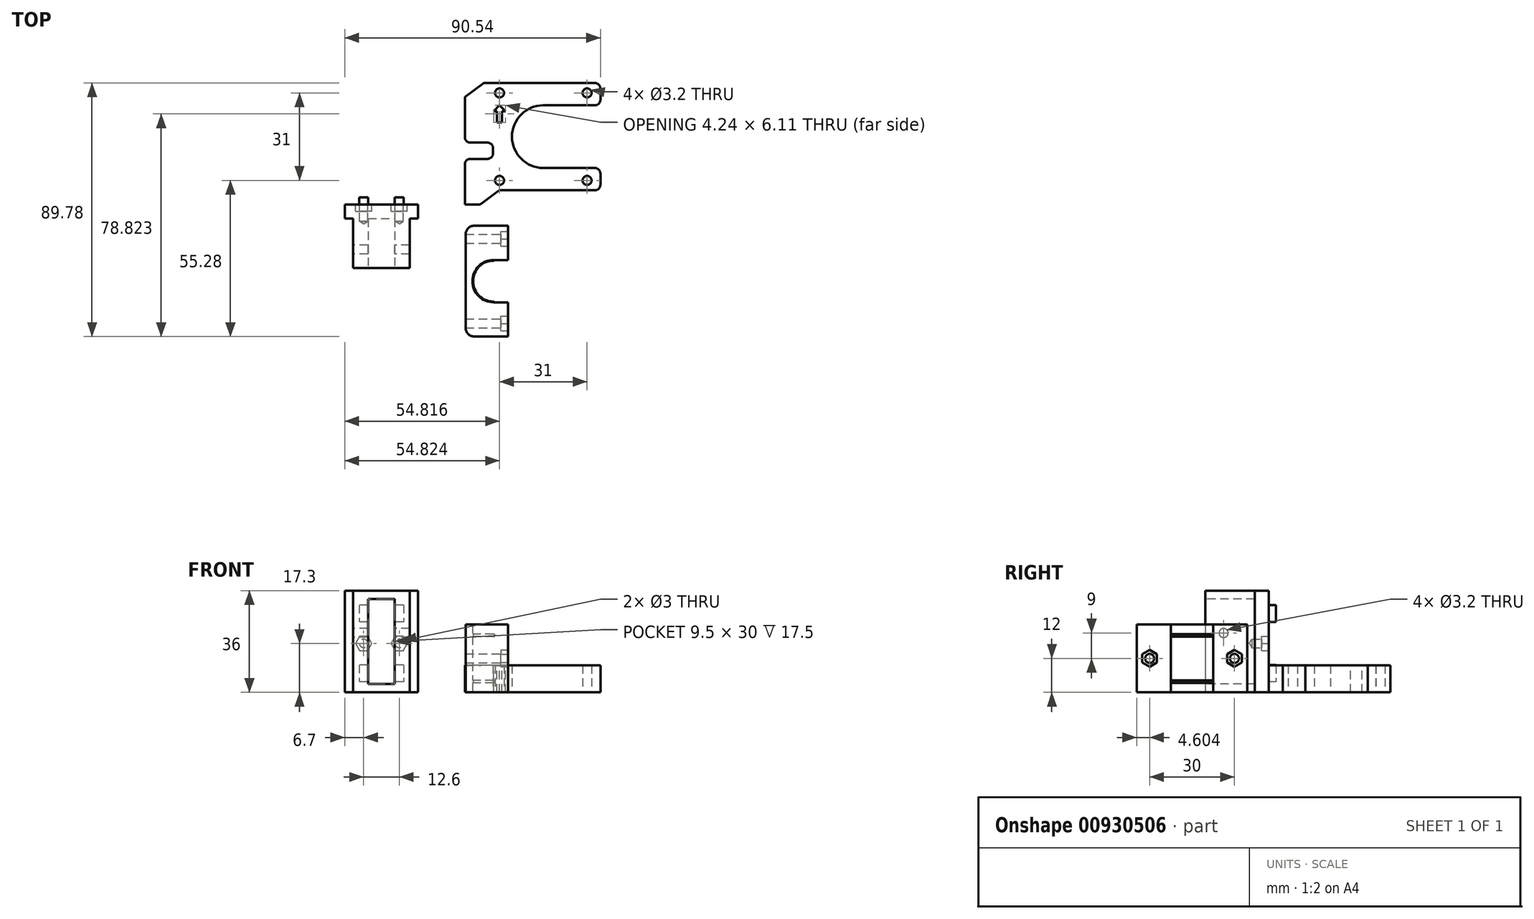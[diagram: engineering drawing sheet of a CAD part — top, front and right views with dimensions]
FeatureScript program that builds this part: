
annotation { "Feature Type Name" : "Feature", "Feature Type Description" : "" }
export const myFeature = defineFeature(function(context is Context, id is Id, definition is map)
    precondition{}
    {
        {
            assignVariable(context, id + "F0", {"name" : "Tolerance", "anyValue" : 0.2});
        }
        {
            var Q0;
            Q0=qCreatedBy(makeId("Top.planeOp"),FACE);
            var sketch = newSketch(context, id + "F1", { "sketchPlane" : qUnion([Q0])});
            skLineSegment(sketch, "E0", {"start": v(7, 16.12) * mm, "end": v(3, 16.12) * mm});
            skLineSegment(sketch, "E1", {"start": v(0, 4.53) * mm, "end": v(0, 0) * mm});
            skLineSegment(sketch, "E2", {"start": v(0, 0) * mm, "end": v(5.2, 0) * mm});
            skLineSegment(sketch, "E3", {"start": v(14.51, 5) * mm, "end": v(46, 5) * mm});
            skArc(sketch, "E4", {"start": v(46, 5) * mm, "mid": v(47.41, 5.59) * mm, "end": v(48, 7) * mm});
            skArc(sketch, "E5", {"start": v(48, 41) * mm, "mid": v(47.41, 42.41) * mm, "end": v(46, 43) * mm});
            skLineSegment(sketch, "E6", {"start": v(46, 43) * mm, "end": v(8.98, 43) * mm});
            skLineSegment(sketch, "E7", {"start": v(3, 21.87) * mm, "end": v(7, 21.87) * mm});
            skCircle(sketch, "E8", {"center": v(12.28, 39.5) * mm, "radius": 1.6 * mm});
            skCircle(sketch, "E9", {"center": v(43.28, 39.5) * mm, "radius": 1.6 * mm});
            skCircle(sketch, "E10", {"center": v(12.28, 8.5) * mm, "radius": 1.6 * mm});
            skCircle(sketch, "E11", {"center": v(43.28, 8.5) * mm, "radius": 1.6 * mm});
            skLineSegment(sketch, "E12", {"start": v(6.37, 42.8) * mm, "end": v(0, 38) * mm});
            skLineSegment(sketch, "E13", {"start": v(11.9, 4.8) * mm, "end": v(5.8, 0.2) * mm});
            skArc(sketch, "E14", {"start": v(6.98, 43) * mm, "mid": v(6.66, 42.95) * mm, "end": v(6.37, 42.8) * mm});
            skArc(sketch, "E15", {"start": v(12.51, 5) * mm, "mid": v(12.2, 4.95) * mm, "end": v(11.9, 4.8) * mm});
            skArc(sketch, "E16", {"start": v(5.2, 0) * mm, "mid": v(5.52, 0.05) * mm, "end": v(5.8, 0.2) * mm});
            skLineSegment(sketch, "E17", {"start": v(0, 38) * mm, "end": v(0, 33.47) * mm});
            skLineSegment(sketch, "E18", {"start": v(14.51, 5) * mm, "end": v(12.5, 5) * mm});
            skLineSegment(sketch, "E19", {"start": v(8.98, 43) * mm, "end": v(7.12, 43) * mm});
            skLineSegment(sketch, "E20", {"start": v(7.12, 43) * mm, "end": v(6.98, 43) * mm});
            skLineSegment(sketch, "E21", {"start": v(6.98, 43) * mm, "end": v(6.98, 43) * mm});
            skLineSegment(sketch, "E22", {"start": v(0, 4.53) * mm, "end": v(0, 12.27) * mm});
            skLineSegment(sketch, "E23", {"start": v(0, 25.73) * mm, "end": v(0, 33.47) * mm});
            skPoint(sketch, "E24", {"position": v(0, 16.12) * mm});
            skPoint(sketch, "E25", {"position": v(0, 21.87) * mm});
            skLineSegment(sketch, "E26", {"start": v(2, 16.12) * mm, "end": v(3, 16.12) * mm});
            skLineSegment(sketch, "E27", {"start": v(0, 14.12) * mm, "end": v(0, 12.27) * mm});
            skLineSegment(sketch, "E28", {"start": v(3, 21.87) * mm, "end": v(2, 21.87) * mm});
            skLineSegment(sketch, "E29", {"start": v(0, 25.73) * mm, "end": v(0, 23.87) * mm});
            skLineSegment(sketch, "E30", {"start": v(7, 16.12) * mm, "end": v(8, 16.12) * mm});
            skLineSegment(sketch, "E31", {"start": v(7, 21.87) * mm, "end": v(8, 21.87) * mm});
            skLineSegment(sketch, "E32", {"start": v(10, 18.12) * mm, "end": v(10, 19.87) * mm});
            skPoint(sketch, "E33", {"position": v(27.78, 12.9) * mm});
            skPoint(sketch, "E34", {"position": v(27.78, 35.1) * mm});
            skLineSegment(sketch, "E35", {"start": v(27.78, 35.1) * mm, "end": v(46, 35.1) * mm});
            skLineSegment(sketch, "E36", {"start": v(27.78, 12.9) * mm, "end": v(46, 12.9) * mm});
            skPoint(sketch, "E37", {"position": v(27.78, 24) * mm});
            skArc(sketch, "E38", {"start": v(27.78, 12.9) * mm, "mid": v(16.68, 24) * mm, "end": v(27.78, 35.1) * mm});
            skLineSegment(sketch, "E39", {"start": v(48, 10.9) * mm, "end": v(48, 7) * mm});
            skLineSegment(sketch, "E40", {"start": v(48, 37.1) * mm, "end": v(48, 41) * mm});
            skPoint(sketch, "E41.visualSharp", {"position": v(48, 12.9) * mm});
            skArc(sketch, "E41.filletArc", {"start": v(48, 10.9) * mm, "mid": v(47.41, 12.31) * mm, "end": v(46, 12.9) * mm});
            skPoint(sketch, "E42.visualSharp", {"position": v(48, 35.1) * mm});
            skArc(sketch, "E42.filletArc", {"start": v(46, 35.1) * mm, "mid": v(47.41, 35.69) * mm, "end": v(48, 37.1) * mm});
            skPoint(sketch, "E43.visualSharp", {"position": v(10, 16.12) * mm});
            skArc(sketch, "E43.filletArc", {"start": v(8, 16.12) * mm, "mid": v(9.41, 16.71) * mm, "end": v(10, 18.12) * mm});
            skPoint(sketch, "E44.visualSharp", {"position": v(10, 21.87) * mm});
            skArc(sketch, "E44.filletArc", {"start": v(10, 19.87) * mm, "mid": v(9.41, 21.29) * mm, "end": v(8, 21.87) * mm});
            skArc(sketch, "E45.filletArc", {"start": v(2, 16.12) * mm, "mid": v(0.59, 15.54) * mm, "end": v(0, 14.12) * mm});
            skArc(sketch, "E46.filletArc", {"start": v(0, 23.87) * mm, "mid": v(0.59, 22.46) * mm, "end": v(2, 21.87) * mm});
            skSolve(sketch);
        }
        {
            var Q0;
            Q0 = qSketchRegion(id + "F1", true);
            extrude(context, id + "F2", {"entities" : qUnion([Q0]), "depth" : 9.6 * mm, "offsetDistance" : 25 * mm});
        }
        {
            var Q0;
            Q0=makeQuery(id+"F2.opExtrude","CAP_FACE",FACE,{"disambiguationData":[OSD([sQuery(id+"F1.wireOp",EDGE,"E0"),sQuery(id+"F1.wireOp",EDGE,"E1"),sQuery(id+"F1.wireOp",EDGE,"E2"),sQuery(id+"F1.wireOp",EDGE,"E3"),sQuery(id+"F1.wireOp",EDGE,"E4"),sQuery(id+"F1.wireOp",EDGE,"E5"),sQuery(id+"F1.wireOp",EDGE,"E6"),sQuery(id+"F1.wireOp",EDGE,"E7"),sQuery(id+"F1.wireOp",EDGE,"E8"),sQuery(id+"F1.wireOp",EDGE,"E9"),sQuery(id+"F1.wireOp",EDGE,"E10"),sQuery(id+"F1.wireOp",EDGE,"E11"),sQuery(id+"F1.wireOp",EDGE,"E12"),sQuery(id+"F1.wireOp",EDGE,"E13"),sQuery(id+"F1.wireOp",EDGE,"E14"),sQuery(id+"F1.wireOp",EDGE,"E15"),sQuery(id+"F1.wireOp",EDGE,"E16"),sQuery(id+"F1.wireOp",EDGE,"E17"),sQuery(id+"F1.wireOp",EDGE,"E18"),sQuery(id+"F1.wireOp",EDGE,"E19"),sQuery(id+"F1.wireOp",EDGE,"E20"),sQuery(id+"F1.wireOp",EDGE,"E21"),sQuery(id+"F1.wireOp",EDGE,"E22"),sQuery(id+"F1.wireOp",EDGE,"E23"),sQuery(id+"F1.wireOp",EDGE,"E26"),sQuery(id+"F1.wireOp",EDGE,"E27"),sQuery(id+"F1.wireOp",EDGE,"E28"),sQuery(id+"F1.wireOp",EDGE,"E29"),sQuery(id+"F1.wireOp",EDGE,"E30"),sQuery(id+"F1.wireOp",EDGE,"E31"),sQuery(id+"F1.wireOp",EDGE,"E32"),sQuery(id+"F1.wireOp",EDGE,"E35"),sQuery(id+"F1.wireOp",EDGE,"E36"),sQuery(id+"F1.wireOp",EDGE,"E38"),sQuery(id+"F1.wireOp",EDGE,"E39"),sQuery(id+"F1.wireOp",EDGE,"E40"),sQuery(id+"F1.wireOp",EDGE,"E41.filletArc"),sQuery(id+"F1.wireOp",EDGE,"E42.filletArc"),sQuery(id+"F1.wireOp",EDGE,"E43.filletArc"),sQuery(id+"F1.wireOp",EDGE,"E44.filletArc"),sQuery(id+"F1.wireOp",EDGE,"E45.filletArc"),sQuery(id+"F1.wireOp",EDGE,"E46.filletArc")])],"isStart":false});
            var sketch = newSketch(context, id + "F3", { "sketchPlane" : qUnion([Q0])});
            skPoint(sketch, "E47", {"position": v(12.28, 39.5) * mm});
            skPoint(sketch, "E48", {"position": v(12.28, 35.1) * mm});
            skLineSegment(sketch, "E49", {"start": v(12.28, 35.1) * mm, "end": v(10.16, 32.99) * mm});
            skLineSegment(sketch, "E50", {"start": v(12.28, 35.1) * mm, "end": v(14.4, 32.97) * mm});
            skLineSegment(sketch, "E51", {"start": v(14.4, 32.97) * mm, "end": v(13.15, 32.97) * mm});
            skLineSegment(sketch, "E52", {"start": v(10.16, 32.99) * mm, "end": v(11.4, 32.99) * mm});
            skLineSegment(sketch, "E53", {"start": v(11.4, 32.99) * mm, "end": v(11.4, 28.99) * mm});
            skLineSegment(sketch, "E54", {"start": v(11.4, 28.99) * mm, "end": v(13.15, 28.99) * mm});
            skLineSegment(sketch, "E55", {"start": v(13.15, 28.99) * mm, "end": v(13.15, 32.97) * mm});
            skSolve(sketch);
        }
        {
            var Q0;
            Q0 = qSketchRegion(id + "F3", true);
            extrude(context, id + "F4", {"entities" : qUnion([Q0]), "operationType" : NewBodyOperationType.REMOVE, "endBound" : BoundingType.THROUGH_ALL, "oppositeDirection" : true, "depth" : 1 * mm, "offsetDistance" : 25 * mm});
        }
        {
            var Q0;
            Q0=qCreatedBy(makeId("Top.planeOp"),FACE);
            var sketch = newSketch(context, id + "F5", { "sketchPlane" : qUnion([Q0])});
            skLineSegment(sketch, "E56", {"start": v(15.27, -34.68) * mm, "end": v(10.17, -34.68) * mm});
            skArc(sketch, "E57", {"start": v(10.17, -19.68) * mm, "mid": v(2.67, -27.18) * mm, "end": v(10.17, -34.68) * mm});
            skLineSegment(sketch, "E58", {"start": v(10.17, -19.68) * mm, "end": v(15.27, -19.68) * mm});
            skLineSegment(sketch, "E59", {"start": v(15.27, -7.58) * mm, "end": v(3.26, -7.58) * mm});
            skArc(sketch, "E60", {"start": v(3.26, -7.58) * mm, "mid": v(1.14, -8.45) * mm, "end": v(0.26, -10.58) * mm});
            skLineSegment(sketch, "E61", {"start": v(0.26, -10.58) * mm, "end": v(0.26, -43.78) * mm});
            skArc(sketch, "E62", {"start": v(0.26, -43.78) * mm, "mid": v(1.14, -45.9) * mm, "end": v(3.26, -46.78) * mm});
            skLineSegment(sketch, "E63", {"start": v(3.26, -46.78) * mm, "end": v(15.27, -46.78) * mm});
            skLineSegment(sketch, "E64", {"start": v(15.27, -19.68) * mm, "end": v(15.27, -7.58) * mm});
            skLineSegment(sketch, "E65", {"start": v(15.27, -34.68) * mm, "end": v(15.27, -46.78) * mm});
            skSolve(sketch);
        }
        {
            var Q0;
            Q0=makeQuery(id+"F5.imprint","IMPRINT",FACE,{"disambiguationData":[TD([[makeQuery(id+"F5.imprint","IMPRINT",EDGE,{"derivedFrom":sQuery(id+"F5.wireOp",EDGE,"E56")}),1.0]])]});
            extrude(context, id + "F6", {"entities" : qUnion([Q0]), "depth" : (3.25 + getVariable(context, 'Tolerance') / 2) * mm, "offsetDistance" : 25 * mm});
        }
        {
            var Q0;
            Q0=makeQuery(id+"F6.opExtrude","CAP_FACE",FACE,{"disambiguationData":[OSD([sQuery(id+"F5.wireOp",EDGE,"E56"),sQuery(id+"F5.wireOp",EDGE,"E57"),sQuery(id+"F5.wireOp",EDGE,"E58"),sQuery(id+"F5.wireOp",EDGE,"E59"),sQuery(id+"F5.wireOp",EDGE,"E60"),sQuery(id+"F5.wireOp",EDGE,"E61"),sQuery(id+"F5.wireOp",EDGE,"E62"),sQuery(id+"F5.wireOp",EDGE,"E63"),sQuery(id+"F5.wireOp",EDGE,"E64"),sQuery(id+"F5.wireOp",EDGE,"E65")])],"isStart":false});
            var sketch = newSketch(context, id + "F7", { "sketchPlane" : qUnion([Q0])});
            skArc(sketch, "E66", {"start": v(10.17, -19.93) * mm, "mid": v(2.92, -27.18) * mm, "end": v(10.17, -34.43) * mm});
            skLineSegment(sketch, "E67", {"start": v(3.26, -7.58) * mm, "end": v(15.27, -7.58) * mm});
            skLineSegment(sketch, "E68", {"start": v(3.26, -46.78) * mm, "end": v(15.27, -46.78) * mm});
            skArc(sketch, "E69", {"start": v(3.26, -7.58) * mm, "mid": v(1.14, -8.45) * mm, "end": v(0.26, -10.58) * mm});
            skArc(sketch, "E70", {"start": v(3.26, -46.78) * mm, "mid": v(1.14, -45.9) * mm, "end": v(0.26, -43.78) * mm});
            skLineSegment(sketch, "E71", {"start": v(0.26, -43.78) * mm, "end": v(0.26, -10.58) * mm});
            skLineSegment(sketch, "E72", {"start": v(10.17, -34.43) * mm, "end": v(10.17, -34.68) * mm});
            skLineSegment(sketch, "E73", {"start": v(10.17, -34.68) * mm, "end": v(15.27, -34.68) * mm});
            skLineSegment(sketch, "E74", {"start": v(15.27, -34.68) * mm, "end": v(15.27, -46.78) * mm});
            skLineSegment(sketch, "E75", {"start": v(10.17, -19.93) * mm, "end": v(10.17, -19.68) * mm});
            skLineSegment(sketch, "E76", {"start": v(10.17, -19.68) * mm, "end": v(15.27, -19.68) * mm});
            skLineSegment(sketch, "E77", {"start": v(15.27, -19.68) * mm, "end": v(15.27, -7.58) * mm});
            skArc(sketch, "E78", {"start": v(10.17, -34.43) * mm, "mid": v(10.35, -34.5) * mm, "end": v(10.42, -34.68) * mm});
            skArc(sketch, "E79", {"start": v(10.17, -19.93) * mm, "mid": v(10.35, -19.85) * mm, "end": v(10.42, -19.68) * mm});
            skSolve(sketch);
        }
        {
            var Q0;
            Q0 = qSketchRegion(id + "F7", true);
            extrude(context, id + "F8", {"entities" : qUnion([Q0]), "operationType" : NewBodyOperationType.ADD, "depth" : (1.1 - getVariable(context, 'Tolerance')) * mm, "offsetDistance" : 25 * mm});
        }
        {
            var Q0;
            Q0=makeQuery(id+"F8.opExtrude","CAP_FACE",FACE,{"disambiguationData":[OSD([sQuery(id+"F7.wireOp",EDGE,"E66"),sQuery(id+"F7.wireOp",EDGE,"E67"),sQuery(id+"F7.wireOp",EDGE,"E68"),sQuery(id+"F7.wireOp",EDGE,"E69"),sQuery(id+"F7.wireOp",EDGE,"E70"),sQuery(id+"F7.wireOp",EDGE,"E71"),sQuery(id+"F7.wireOp",EDGE,"E73"),sQuery(id+"F7.wireOp",EDGE,"E74"),sQuery(id+"F7.wireOp",EDGE,"E76"),sQuery(id+"F7.wireOp",EDGE,"E77"),sQuery(id+"F7.wireOp",EDGE,"E78"),sQuery(id+"F7.wireOp",EDGE,"E79")])],"isStart":false});
            var sketch = newSketch(context, id + "F9", { "sketchPlane" : qUnion([Q0])});
            skArc(sketch, "E80", {"start": v(10.17, -19.68) * mm, "mid": v(2.67, -27.18) * mm, "end": v(10.17, -34.68) * mm});
            skLineSegment(sketch, "E81", {"start": v(10.17, -34.68) * mm, "end": v(15.27, -34.68) * mm});
            skLineSegment(sketch, "E82", {"start": v(10.17, -19.68) * mm, "end": v(15.27, -19.68) * mm});
            skLineSegment(sketch, "E83", {"start": v(15.27, -19.68) * mm, "end": v(15.27, -7.58) * mm});
            skLineSegment(sketch, "E84", {"start": v(15.27, -34.68) * mm, "end": v(15.27, -46.78) * mm});
            skLineSegment(sketch, "E85", {"start": v(15.27, -46.78) * mm, "end": v(3.26, -46.78) * mm});
            skLineSegment(sketch, "E86", {"start": v(15.27, -7.58) * mm, "end": v(3.26, -7.58) * mm});
            skArc(sketch, "E87", {"start": v(3.26, -7.58) * mm, "mid": v(1.14, -8.45) * mm, "end": v(0.26, -10.58) * mm});
            skArc(sketch, "E88", {"start": v(3.26, -46.78) * mm, "mid": v(1.14, -45.9) * mm, "end": v(0.26, -43.78) * mm});
            skLineSegment(sketch, "E89", {"start": v(0.26, -43.78) * mm, "end": v(0.26, -10.58) * mm});
            skSolve(sketch);
        }
        {
            var Q0;
            Q0 = qSketchRegion(id + "F9", true);
            extrude(context, id + "F10", {"entities" : qUnion([Q0]), "operationType" : NewBodyOperationType.ADD, "depth" : (15.3 + getVariable(context, 'Tolerance')) * mm, "offsetDistance" : 25 * mm});
        }
        {
            var Q0;
            Q0=makeQuery(id+"F10.opExtrude","CAP_FACE",FACE,{"disambiguationData":[OSD([sQuery(id+"F9.wireOp",EDGE,"E80"),sQuery(id+"F9.wireOp",EDGE,"E81"),sQuery(id+"F9.wireOp",EDGE,"E82"),sQuery(id+"F9.wireOp",EDGE,"E83"),sQuery(id+"F9.wireOp",EDGE,"E84"),sQuery(id+"F9.wireOp",EDGE,"E85"),sQuery(id+"F9.wireOp",EDGE,"E86"),sQuery(id+"F9.wireOp",EDGE,"E87"),sQuery(id+"F9.wireOp",EDGE,"E88"),sQuery(id+"F9.wireOp",EDGE,"E89")])],"isStart":false});
            var sketch = newSketch(context, id + "F11", { "sketchPlane" : qUnion([Q0])});
            skArc(sketch, "E90", {"start": v(10.17, -19.93) * mm, "mid": v(2.92, -27.18) * mm, "end": v(10.17, -34.43) * mm});
            skArc(sketch, "E91", {"start": v(10.17, -34.43) * mm, "mid": v(10.35, -34.5) * mm, "end": v(10.42, -34.68) * mm});
            skArc(sketch, "E92", {"start": v(10.17, -19.93) * mm, "mid": v(10.35, -19.85) * mm, "end": v(10.42, -19.68) * mm});
            skLineSegment(sketch, "E93", {"start": v(10.42, -19.68) * mm, "end": v(15.27, -19.68) * mm});
            skLineSegment(sketch, "E94", {"start": v(10.42, -34.68) * mm, "end": v(15.27, -34.68) * mm});
            skLineSegment(sketch, "E95", {"start": v(15.27, -34.68) * mm, "end": v(15.27, -46.78) * mm});
            skLineSegment(sketch, "E96", {"start": v(15.27, -46.78) * mm, "end": v(3.26, -46.78) * mm});
            skLineSegment(sketch, "E97", {"start": v(15.27, -19.68) * mm, "end": v(15.27, -7.58) * mm});
            skLineSegment(sketch, "E98", {"start": v(15.27, -7.58) * mm, "end": v(3.26, -7.58) * mm});
            skArc(sketch, "E99", {"start": v(3.26, -7.58) * mm, "mid": v(1.14, -8.45) * mm, "end": v(0.26, -10.58) * mm});
            skArc(sketch, "E100", {"start": v(3.26, -46.78) * mm, "mid": v(1.14, -45.9) * mm, "end": v(0.26, -43.78) * mm});
            skLineSegment(sketch, "E101", {"start": v(0.26, -43.78) * mm, "end": v(0.26, -10.58) * mm});
            skSolve(sketch);
        }
        {
            var Q0;
            Q0 = qSketchRegion(id + "F11", true);
            extrude(context, id + "F12", {"entities" : qUnion([Q0]), "operationType" : NewBodyOperationType.ADD, "depth" : (1.1 - getVariable(context, 'Tolerance')) * mm, "offsetDistance" : 25 * mm});
        }
        {
            var Q0;
            Q0=makeQuery(id+"F12.opExtrude","CAP_FACE",FACE,{"disambiguationData":[OSD([sQuery(id+"F11.wireOp",EDGE,"E90"),sQuery(id+"F11.wireOp",EDGE,"E91"),sQuery(id+"F11.wireOp",EDGE,"E92"),sQuery(id+"F11.wireOp",EDGE,"E93"),sQuery(id+"F11.wireOp",EDGE,"E94"),sQuery(id+"F11.wireOp",EDGE,"E95"),sQuery(id+"F11.wireOp",EDGE,"E96"),sQuery(id+"F11.wireOp",EDGE,"E97"),sQuery(id+"F11.wireOp",EDGE,"E98"),sQuery(id+"F11.wireOp",EDGE,"E99"),sQuery(id+"F11.wireOp",EDGE,"E100"),sQuery(id+"F11.wireOp",EDGE,"E101")])],"isStart":false});
            var sketch = newSketch(context, id + "F13", { "sketchPlane" : qUnion([Q0])});
            skArc(sketch, "E102", {"start": v(10.17, -19.68) * mm, "mid": v(2.67, -27.18) * mm, "end": v(10.17, -34.68) * mm});
            skLineSegment(sketch, "E103", {"start": v(10.17, -34.68) * mm, "end": v(15.27, -34.68) * mm});
            skLineSegment(sketch, "E104", {"start": v(10.17, -19.68) * mm, "end": v(15.27, -19.68) * mm});
            skLineSegment(sketch, "E105", {"start": v(15.27, -19.68) * mm, "end": v(15.27, -7.58) * mm});
            skLineSegment(sketch, "E106", {"start": v(15.27, -7.58) * mm, "end": v(3.26, -7.58) * mm});
            skLineSegment(sketch, "E107", {"start": v(15.27, -34.68) * mm, "end": v(15.27, -46.78) * mm});
            skLineSegment(sketch, "E108", {"start": v(15.27, -46.78) * mm, "end": v(3.26, -46.78) * mm});
            skArc(sketch, "E109", {"start": v(3.26, -46.78) * mm, "mid": v(1.14, -45.9) * mm, "end": v(0.26, -43.78) * mm});
            skArc(sketch, "E110", {"start": v(3.26, -7.58) * mm, "mid": v(1.14, -8.45) * mm, "end": v(0.26, -10.58) * mm});
            skLineSegment(sketch, "E111", {"start": v(0.26, -10.58) * mm, "end": v(0.26, -43.78) * mm});
            skSolve(sketch);
        }
        {
            var Q0;
            Q0 = qSketchRegion(id + "F13", true);
            extrude(context, id + "F14", {"entities" : qUnion([Q0]), "operationType" : NewBodyOperationType.ADD, "depth" : (3.25 + (getVariable(context, 'Tolerance') / 2)) * mm, "offsetDistance" : 25 * mm});
        }
        {
            var Q0;
            Q0=makeQuery(id+"F14.boolean.opBoolean","MERGE",FACE,{"derivedFrom":[makeQuery(id+"F12.boolean.opBoolean","MERGE",FACE,{"derivedFrom":[makeQuery(id+"F10.boolean.opBoolean","MERGE",FACE,{"derivedFrom":[makeQuery(id+"F8.boolean.opBoolean","MERGE",FACE,{"derivedFrom":[makeQuery(id+"F6.opExtrude","SWEPT_FACE",FACE,{"disambiguationData":[OSD([sQuery(id+"F5.wireOp",EDGE,"E64")])]}),makeQuery(id+"F8.opExtrude","SWEPT_FACE",FACE,{"disambiguationData":[OSD([sQuery(id+"F7.wireOp",EDGE,"E77")])]})]}),makeQuery(id+"F10.opExtrude","SWEPT_FACE",FACE,{"disambiguationData":[OSD([sQuery(id+"F9.wireOp",EDGE,"E83")])]})]}),makeQuery(id+"F12.opExtrude","SWEPT_FACE",FACE,{"disambiguationData":[OSD([sQuery(id+"F11.wireOp",EDGE,"E97")])]})]}),makeQuery(id+"F14.opExtrude","SWEPT_FACE",FACE,{"disambiguationData":[OSD([sQuery(id+"F13.wireOp",EDGE,"E105")])]})]});
            var sketch = newSketch(context, id + "F15", { "sketchPlane" : qUnion([Q0])});
            skPoint(sketch, "E112", {"position": v(-12.18, 12) * mm});
            skPoint(sketch, "E113", {"position": v(-42.18, 12) * mm});
            skCircle(sketch, "E114.cCircle", {"center": v(-42.18, 12) * mm, "radius": 2.6 * mm, "construction": true});
            skLineSegment(sketch, "E114.0", {"start": v(-42.18, 15) * mm, "end": v(-39.58, 13.5) * mm});
            skLineSegment(sketch, "E114.1", {"start": v(-39.58, 13.5) * mm, "end": v(-39.58, 10.5) * mm});
            skLineSegment(sketch, "E114.2", {"start": v(-39.58, 10.5) * mm, "end": v(-42.18, 9) * mm});
            skLineSegment(sketch, "E114.3", {"start": v(-42.18, 9) * mm, "end": v(-44.77, 10.5) * mm});
            skLineSegment(sketch, "E114.4", {"start": v(-44.77, 10.5) * mm, "end": v(-44.77, 13.5) * mm});
            skLineSegment(sketch, "E114.5", {"start": v(-44.77, 13.5) * mm, "end": v(-42.18, 15) * mm});
            skPoint(sketch, "E114.0.midPoint", {"position": v(-40.88, 14.25) * mm});
            skCircle(sketch, "E115.cCircle", {"center": v(-12.18, 12) * mm, "radius": 2.6 * mm, "construction": true});
            skLineSegment(sketch, "E115.0", {"start": v(-12.18, 15) * mm, "end": v(-9.58, 13.5) * mm});
            skLineSegment(sketch, "E115.1", {"start": v(-9.58, 13.5) * mm, "end": v(-9.58, 10.5) * mm});
            skLineSegment(sketch, "E115.2", {"start": v(-9.58, 10.5) * mm, "end": v(-12.18, 9) * mm});
            skLineSegment(sketch, "E115.3", {"start": v(-12.18, 9) * mm, "end": v(-14.77, 10.5) * mm});
            skLineSegment(sketch, "E115.4", {"start": v(-14.77, 10.5) * mm, "end": v(-14.77, 13.5) * mm});
            skLineSegment(sketch, "E115.5", {"start": v(-14.77, 13.5) * mm, "end": v(-12.18, 15) * mm});
            skPoint(sketch, "E115.0.midPoint", {"position": v(-10.88, 14.25) * mm});
            skSolve(sketch);
        }
        {
            var Q0;
            Q0 = qSketchRegion(id + "F15", true);
            extrude(context, id + "F16", {"entities" : qUnion([Q0]), "operationType" : NewBodyOperationType.REMOVE, "oppositeDirection" : true, "depth" : 2.5 * mm, "offsetDistance" : 25 * mm});
        }
        {
            var Q0;
            Q0=sQuery(id+"F15.wireOp",VERTEX,"E113");
            var Q1;
            Q1=sQuery(id+"F15.wireOp",VERTEX,"E112");
            var Q2;
            Q2=makeQuery(id+"F6.opExtrude","SWEPT_BODY",BODY,{"disambiguationData":[OSD([sQuery(id+"F5.wireOp",EDGE,"E56"),sQuery(id+"F5.wireOp",EDGE,"E57"),sQuery(id+"F5.wireOp",EDGE,"E58"),sQuery(id+"F5.wireOp",EDGE,"E59"),sQuery(id+"F5.wireOp",EDGE,"E60"),sQuery(id+"F5.wireOp",EDGE,"E61"),sQuery(id+"F5.wireOp",EDGE,"E62"),sQuery(id+"F5.wireOp",EDGE,"E63"),sQuery(id+"F5.wireOp",EDGE,"E64"),sQuery(id+"F5.wireOp",EDGE,"E65")])]});
            hole(context, id + "F17", {"style" : HoleStyle.SIMPLE, "endStyle" : HoleEndStyle.THROUGH, "holeDiameter" : (3 + getVariable(context, 'Tolerance')) * mm, "majorDiameter" : 5 * mm, "isTappedThrough" : true, "tappedDepth" : 12 * mm, "tapClearance" : 3, "locations" : qUnion([Q0, Q1]), "scope" : qUnion([Q2])});
        }
        {
            var Q0;
            Q0=qCreatedBy(makeId("Top.planeOp"),FACE);
            var sketch = newSketch(context, id + "F18", { "sketchPlane" : qUnion([Q0])});
            skLineSegment(sketch, "E116", {"start": v(-16.54, 0) * mm, "end": v(-42.54, 0) * mm});
            skLineSegment(sketch, "E117", {"start": v(-42.54, 0) * mm, "end": v(-42.54, -5) * mm});
            skLineSegment(sketch, "E118", {"start": v(-16.54, 0) * mm, "end": v(-16.54, -5) * mm});
            skLineSegment(sketch, "E119", {"start": v(-42.54, -5) * mm, "end": v(-39.54, -5) * mm});
            skLineSegment(sketch, "E120", {"start": v(-16.54, -5) * mm, "end": v(-19.54, -5) * mm});
            skLineSegment(sketch, "E121", {"start": v(-39.54, -5) * mm, "end": v(-39.54, -22.5) * mm});
            skLineSegment(sketch, "E122", {"start": v(-19.54, -5) * mm, "end": v(-19.54, -22.5) * mm});
            skLineSegment(sketch, "E123", {"start": v(-39.54, -22.5) * mm, "end": v(-19.54, -22.5) * mm});
            skSolve(sketch);
        }
        {
            var Q0;
            Q0=makeQuery(id+"F18.imprint","IMPRINT",FACE,{"disambiguationData":[TD([[makeQuery(id+"F18.imprint","IMPRINT",EDGE,{"derivedFrom":sQuery(id+"F18.wireOp",EDGE,"E116")}),1.0]])]});
            extrude(context, id + "F19", {"entities" : qUnion([Q0]), "depth" : 36 * mm, "offsetDistance" : 25 * mm});
        }
        {
            var Q0;
            Q0=makeQuery(id+"F19.opExtrude","SWEPT_FACE",FACE,{"disambiguationData":[OSD([sQuery(id+"F18.wireOp",EDGE,"E121")])]});
            var sketch = newSketch(context, id + "F20", { "sketchPlane" : qUnion([Q0])});
            skPoint(sketch, "E124", {"position": v(16, 21) * mm});
            skSolve(sketch);
        }
        {
            var Q0;
            Q0=sQuery(id+"F20.wireOp",VERTEX,"E124");
            var Q1;
            Q1=makeQuery(id+"F19.opExtrude","SWEPT_BODY",BODY,{"disambiguationData":[OSD([sQuery(id+"F18.wireOp",EDGE,"E116"),sQuery(id+"F18.wireOp",EDGE,"E117"),sQuery(id+"F18.wireOp",EDGE,"E118"),sQuery(id+"F18.wireOp",EDGE,"E119"),sQuery(id+"F18.wireOp",EDGE,"E120"),sQuery(id+"F18.wireOp",EDGE,"E121"),sQuery(id+"F18.wireOp",EDGE,"E122"),sQuery(id+"F18.wireOp",EDGE,"E123")])]});
            hole(context, id + "F21", {"style" : HoleStyle.SIMPLE, "endStyle" : HoleEndStyle.THROUGH, "holeDiameter" : (3 + getVariable(context, 'Tolerance')) * mm, "majorDiameter" : 5 * mm, "isTappedThrough" : true, "tappedDepth" : 12 * mm, "tapClearance" : 3, "locations" : qUnion([Q0]), "scope" : qUnion([Q1])});
        }
        {
            var Q0;
            Q0=makeQuery(id+"F19.opExtrude","SWEPT_FACE",FACE,{"disambiguationData":[OSD([sQuery(id+"F18.wireOp",EDGE,"E123")])]});
            var sketch = newSketch(context, id + "F22", { "sketchPlane" : qUnion([Q0])});
            skLineSegment(sketch, "E125.bottom", {"start": v(-34.3, 33) * mm, "end": v(-24.8, 33) * mm});
            skLineSegment(sketch, "E125.top", {"start": v(-34.3, 3) * mm, "end": v(-24.8, 3) * mm});
            skLineSegment(sketch, "E125.left", {"start": v(-34.3, 33) * mm, "end": v(-34.3, 3) * mm});
            skLineSegment(sketch, "E125.right", {"start": v(-24.8, 33) * mm, "end": v(-24.8, 3) * mm});
            skSolve(sketch);
        }
        {
            var Q0;
            Q0 = qSketchRegion(id + "F22", true);
            extrude(context, id + "F23", {"entities" : qUnion([Q0]), "operationType" : NewBodyOperationType.REMOVE, "oppositeDirection" : true, "depth" : 17.5 * mm, "offsetDistance" : 25 * mm});
        }
        {
            var Q0;
            Q0=makeQuery(id+"F19.opExtrude","SWEPT_FACE",FACE,{"disambiguationData":[OSD([sQuery(id+"F18.wireOp",EDGE,"E116")])]});
            var sketch = newSketch(context, id + "F24", { "sketchPlane" : qUnion([Q0])});
            skLineSegment(sketch, "E126.bottom", {"start": v(21.7, 30.9) * mm, "end": v(24.8, 30.9) * mm});
            skLineSegment(sketch, "E126.top", {"start": v(21.7, 24.9) * mm, "end": v(24.8, 24.9) * mm});
            skLineSegment(sketch, "E126.left", {"start": v(21.7, 30.9) * mm, "end": v(21.7, 24.9) * mm});
            skLineSegment(sketch, "E126.right", {"start": v(24.8, 30.9) * mm, "end": v(24.8, 24.9) * mm});
            skLineSegment(sketch, "E127.bottom", {"start": v(34.3, 30.9) * mm, "end": v(37.4, 30.9) * mm});
            skLineSegment(sketch, "E127.top", {"start": v(34.3, 24.9) * mm, "end": v(37.4, 24.9) * mm});
            skLineSegment(sketch, "E127.left", {"start": v(34.3, 30.9) * mm, "end": v(34.3, 24.9) * mm});
            skLineSegment(sketch, "E127.right", {"start": v(37.4, 30.9) * mm, "end": v(37.4, 24.9) * mm});
            skLineSegment(sketch, "E128.bottom", {"start": v(21.7, 9.7) * mm, "end": v(24.8, 9.7) * mm});
            skLineSegment(sketch, "E128.top", {"start": v(21.7, 3.7) * mm, "end": v(24.8, 3.7) * mm});
            skLineSegment(sketch, "E128.left", {"start": v(21.7, 9.7) * mm, "end": v(21.7, 3.7) * mm});
            skLineSegment(sketch, "E128.right", {"start": v(24.8, 9.7) * mm, "end": v(24.8, 3.7) * mm});
            skLineSegment(sketch, "E129.bottom", {"start": v(34.3, 9.7) * mm, "end": v(37.4, 9.7) * mm});
            skLineSegment(sketch, "E129.top", {"start": v(34.3, 3.7) * mm, "end": v(37.4, 3.7) * mm});
            skLineSegment(sketch, "E129.left", {"start": v(34.3, 9.7) * mm, "end": v(34.3, 3.7) * mm});
            skLineSegment(sketch, "E129.right", {"start": v(37.4, 9.7) * mm, "end": v(37.4, 3.7) * mm});
            skPoint(sketch, "E130", {"position": v(23.24, 24.9) * mm});
            skPoint(sketch, "E131", {"position": v(35.84, 24.9) * mm});
            skPoint(sketch, "E132", {"position": v(23.24, 9.7) * mm});
            skPoint(sketch, "E133", {"position": v(35.84, 9.7) * mm});
            skPoint(sketch, "E134", {"position": v(35.84, 17.3) * mm});
            skPoint(sketch, "E135", {"position": v(23.24, 17.3) * mm});
            skSolve(sketch);
        }
        {
            var Q0;
            Q0 = qSketchRegion(id + "F24", true);
            extrude(context, id + "F25", {"entities" : qUnion([Q0]), "operationType" : NewBodyOperationType.ADD, "depth" : 2.5 * mm, "offsetDistance" : 25 * mm});
        }
        {
            var Q0;
            Q0=sQuery(id+"F24.wireOp",VERTEX,"E135");
            var Q1;
            Q1=sQuery(id+"F24.wireOp",VERTEX,"E134");
            var Q2;
            Q2=makeQuery(id+"F19.opExtrude","SWEPT_BODY",BODY,{"disambiguationData":[OSD([sQuery(id+"F18.wireOp",EDGE,"E116"),sQuery(id+"F18.wireOp",EDGE,"E117"),sQuery(id+"F18.wireOp",EDGE,"E118"),sQuery(id+"F18.wireOp",EDGE,"E119"),sQuery(id+"F18.wireOp",EDGE,"E120"),sQuery(id+"F18.wireOp",EDGE,"E121"),sQuery(id+"F18.wireOp",EDGE,"E122"),sQuery(id+"F18.wireOp",EDGE,"E123")])]});
            hole(context, id + "F26", {"style" : HoleStyle.SIMPLE, "endStyle" : HoleEndStyle.BLIND, "holeDiameter" : 3 * mm, "majorDiameter" : 5 * mm, "holeDepth" : 6 * mm, "isTappedThrough" : true, "tappedDepth" : 12 * mm, "tapClearance" : 3, "locations" : qUnion([Q0, Q1]), "scope" : qUnion([Q2])});
        }
        {
            var Q0;
            Q0=makeQuery(id+"F19.opExtrude","SWEPT_FACE",FACE,{"disambiguationData":[OSD([sQuery(id+"F18.wireOp",EDGE,"E116")])]});
            var sketch = newSketch(context, id + "F27", { "sketchPlane" : qUnion([Q0])});
            skCircle(sketch, "E136.cCircle", {"center": v(23.24, 17.3) * mm, "radius": 2.5 * mm, "construction": true});
            skLineSegment(sketch, "E136.0", {"start": v(21.8, 19.8) * mm, "end": v(24.68, 19.8) * mm});
            skLineSegment(sketch, "E136.1", {"start": v(24.68, 19.8) * mm, "end": v(26.13, 17.3) * mm});
            skLineSegment(sketch, "E136.2", {"start": v(26.13, 17.3) * mm, "end": v(24.68, 14.8) * mm});
            skLineSegment(sketch, "E136.3", {"start": v(24.68, 14.8) * mm, "end": v(21.8, 14.8) * mm});
            skLineSegment(sketch, "E136.4", {"start": v(21.8, 14.8) * mm, "end": v(20.35, 17.3) * mm});
            skLineSegment(sketch, "E136.5", {"start": v(20.35, 17.3) * mm, "end": v(21.8, 19.8) * mm});
            skPoint(sketch, "E136.0.midPoint", {"position": v(23.24, 19.8) * mm});
            skCircle(sketch, "E137.cCircle", {"center": v(35.84, 17.3) * mm, "radius": 2.5 * mm, "construction": true});
            skLineSegment(sketch, "E137.0", {"start": v(34.4, 19.8) * mm, "end": v(37.28, 19.8) * mm});
            skLineSegment(sketch, "E137.1", {"start": v(37.28, 19.8) * mm, "end": v(38.73, 17.3) * mm});
            skLineSegment(sketch, "E137.2", {"start": v(38.73, 17.3) * mm, "end": v(37.28, 14.8) * mm});
            skLineSegment(sketch, "E137.3", {"start": v(37.28, 14.8) * mm, "end": v(34.4, 14.8) * mm});
            skLineSegment(sketch, "E137.4", {"start": v(34.4, 14.8) * mm, "end": v(32.95, 17.3) * mm});
            skLineSegment(sketch, "E137.5", {"start": v(32.95, 17.3) * mm, "end": v(34.4, 19.8) * mm});
            skPoint(sketch, "E137.0.midPoint", {"position": v(35.84, 19.8) * mm});
            skSolve(sketch);
        }
        {
            var Q0;
            Q0 = qSketchRegion(id + "F27", true);
            extrude(context, id + "F28", {"entities" : qUnion([Q0]), "operationType" : NewBodyOperationType.REMOVE, "oppositeDirection" : true, "depth" : 2.5 * mm, "offsetDistance" : 25 * mm});
        }
    });
